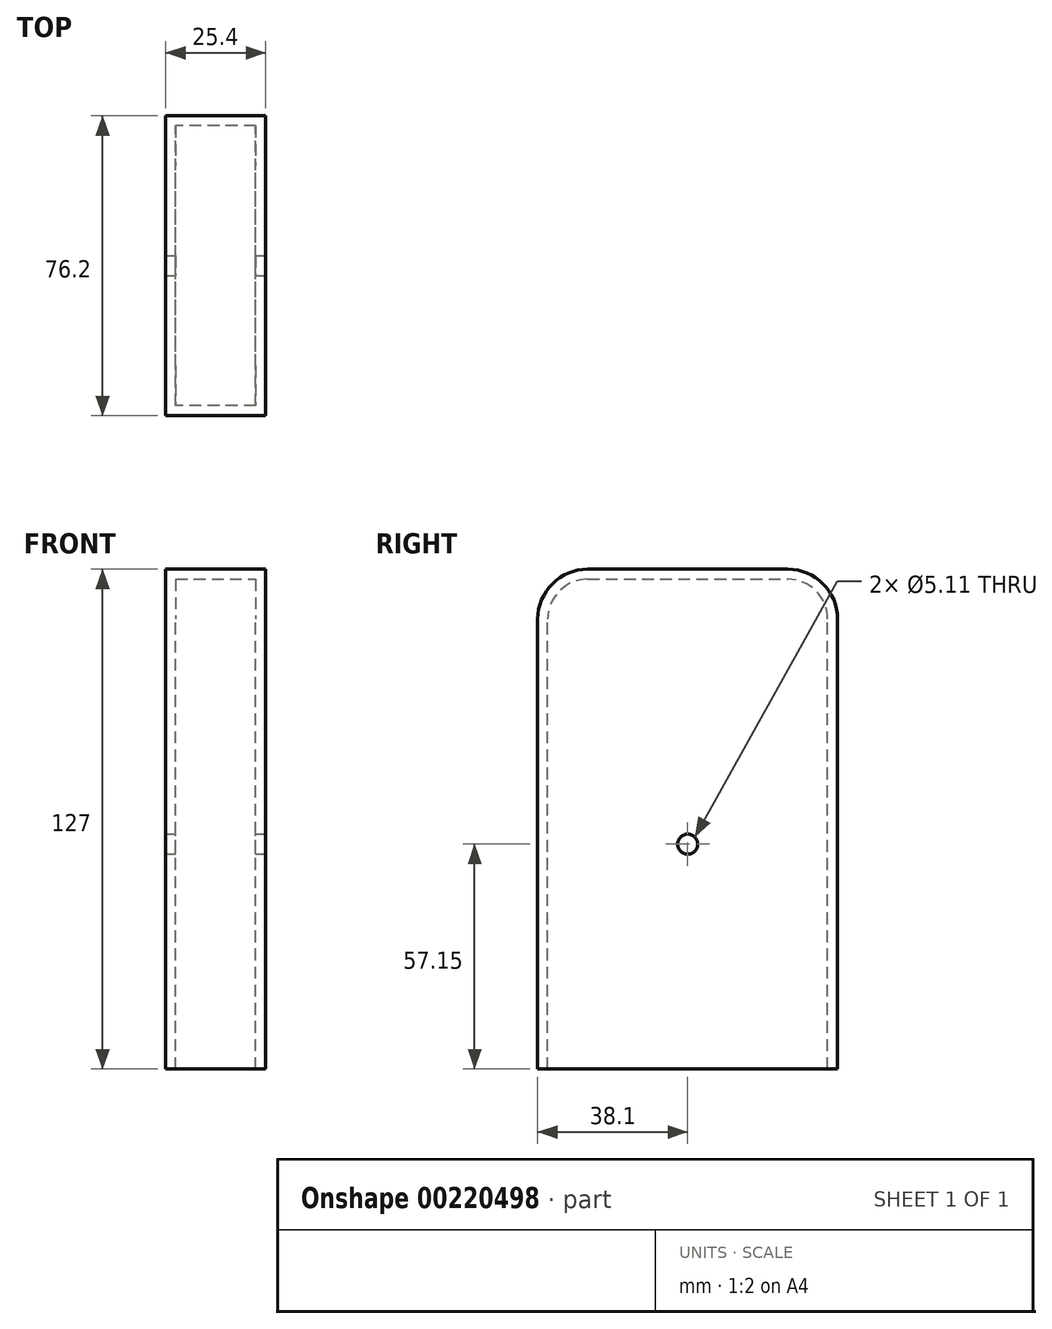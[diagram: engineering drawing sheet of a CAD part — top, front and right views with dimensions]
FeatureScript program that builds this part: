
annotation { "Feature Type Name" : "Feature", "Feature Type Description" : "" }
export const myFeature = defineFeature(function(context is Context, id is Id, definition is map)
    precondition{}
    {
        {
            var Q0;
            Q0=qCreatedBy(makeId("Top.planeOp"),FACE);
            var sketch = newSketch(context, id + "F0", { "sketchPlane" : qUnion([Q0])});
            skLineSegment(sketch, "E0.bottom", {"start": v(63.5, -38.1) * mm, "end": v(-63.5, -38.1) * mm});
            skLineSegment(sketch, "E0.top", {"start": v(63.5, 38.1) * mm, "end": v(-63.5, 38.1) * mm});
            skLineSegment(sketch, "E0.left", {"start": v(63.5, -38.1) * mm, "end": v(63.5, 38.1) * mm});
            skLineSegment(sketch, "E0.right", {"start": v(-63.5, -38.1) * mm, "end": v(-63.5, 38.1) * mm});
            skPoint(sketch, "E0.middle", {"position": v(0, 0) * mm});
            skSolve(sketch);
        }
        {
            var Q0;
            Q0 = qSketchRegion(id + "F0", true);
            extrude(context, id + "F1", {"entities" : qUnion([Q0]), "depth" : 25.4 * mm});
        }
        {
            var Q0;
            Q0=makeQuery(id+"F1.opExtrude","SWEPT_FACE",FACE,{"disambiguationData":[OSD([sQuery(id+"F0.wireOp",EDGE,"E0.bottom")])]});
            var sketch = newSketch(context, id + "F2", { "sketchPlane" : qUnion([Q0])});
            skLineSegment(sketch, "E1", {"start": v(0, 37.96) * mm, "end": v(0, -11.59) * mm});
            skPoint(sketch, "E1.startSnap0", {"position": v(0, 25.4) * mm});
            skSolve(sketch);
        }
        {
            var Q0;
            Q0=makeQuery(id+"F1.opExtrude","SWEPT_EDGE",EDGE,{"disambiguationData":[OSD([sQuery(id+"F0.wireOp",EDGE,"E0.bottom"),sQuery(id+"F0.wireOp",EDGE,"E0.right")])]});
            var Q1;
            Q1=makeQuery(id+"F1.opExtrude","SWEPT_EDGE",EDGE,{"disambiguationData":[OSD([sQuery(id+"F0.wireOp",EDGE,"E0.top"),sQuery(id+"F0.wireOp",EDGE,"E0.right")])]});
            fillet(context, id + "F3", {"entities" : qUnion([Q0, Q1]), "radius" : 12.7 * mm, "tangentPropagation" : true, "allowEdgeOverflow" : false});
        }
        {
            var Q0;
            Q0=makeQuery(id+"F1.opExtrude","SWEPT_FACE",FACE,{"disambiguationData":[OSD([sQuery(id+"F0.wireOp",EDGE,"E0.left")])]});
            shell(context, id + "F4", {"entities" : qUnion([Q0]), "thickness" : 2.54 * mm});
        }
        {
            var Q0;
            Q0=makeQuery(id+"F1.opExtrude","CAP_FACE",FACE,{"disambiguationData":[OSD([sQuery(id+"F0.wireOp",EDGE,"E0.bottom"),sQuery(id+"F0.wireOp",EDGE,"E0.top"),sQuery(id+"F0.wireOp",EDGE,"E0.left"),sQuery(id+"F0.wireOp",EDGE,"E0.right")])],"isStart":false});
            var sketch = newSketch(context, id + "F5", { "sketchPlane" : qUnion([Q0])});
            skPoint(sketch, "E2", {"position": v(6.35, 0) * mm});
            skSolve(sketch);
        }
        {
            var Q0;
            Q0=sQuery(id+"F5.wireOp",VERTEX,"E2");
            var Q1;
            Q1=makeQuery(id+"F1.opExtrude","SWEPT_BODY",BODY,{"disambiguationData":[OSD([sQuery(id+"F0.wireOp",EDGE,"E0.bottom"),sQuery(id+"F0.wireOp",EDGE,"E0.top"),sQuery(id+"F0.wireOp",EDGE,"E0.left"),sQuery(id+"F0.wireOp",EDGE,"E0.right")])]});
            hole(context, id + "F6", {"style" : HoleStyle.SIMPLE, "endStyle" : HoleEndStyle.THROUGH, "standardTappedOrClearance" : lookupTablePath({ "standard" : "ANSI", "fit" : "Normal (ASME)", "size" : "#10", "type" : "Clearance" }), "standardBlindInLast" : lookupTablePath({ "fit" : "Free", "standard" : "ANSI", "size" : "#10", "type" : "Clearance" }), "holeDiameter" : 5.1 * mm, "locations" : qUnion([Q0]), "scope" : qUnion([Q1]), "isTappedThrough" : true});
        }
        {
            var Q0;
            Q0=makeQuery(id+"F1.opExtrude","SWEPT_BODY",BODY,{"disambiguationData":[OSD([sQuery(id+"F0.wireOp",EDGE,"E0.bottom"),sQuery(id+"F0.wireOp",EDGE,"E0.top"),sQuery(id+"F0.wireOp",EDGE,"E0.left"),sQuery(id+"F0.wireOp",EDGE,"E0.right")])]});
            var Q1;
            Q1=makeQuery(id+"F1.opExtrude","CAP_EDGE",EDGE,{"disambiguationData":[OSD([sQuery(id+"F0.wireOp",EDGE,"E0.left")])],"isStart":false});
            var Q2;
            Q2=makeQuery(id+"F1.opExtrude","CAP_EDGE",EDGE,{"disambiguationData":[OSD([sQuery(id+"F0.wireOp",EDGE,"E0.left")])],"isStart":false});
            transform(context, id + "F7", {"entities" : qUnion([Q0]), "transformType" : TransformType.ROTATION, "transformAxis" : qUnion([Q2]), "angle" : 90 * degree, "makeCopy" : false});
        }
    });
